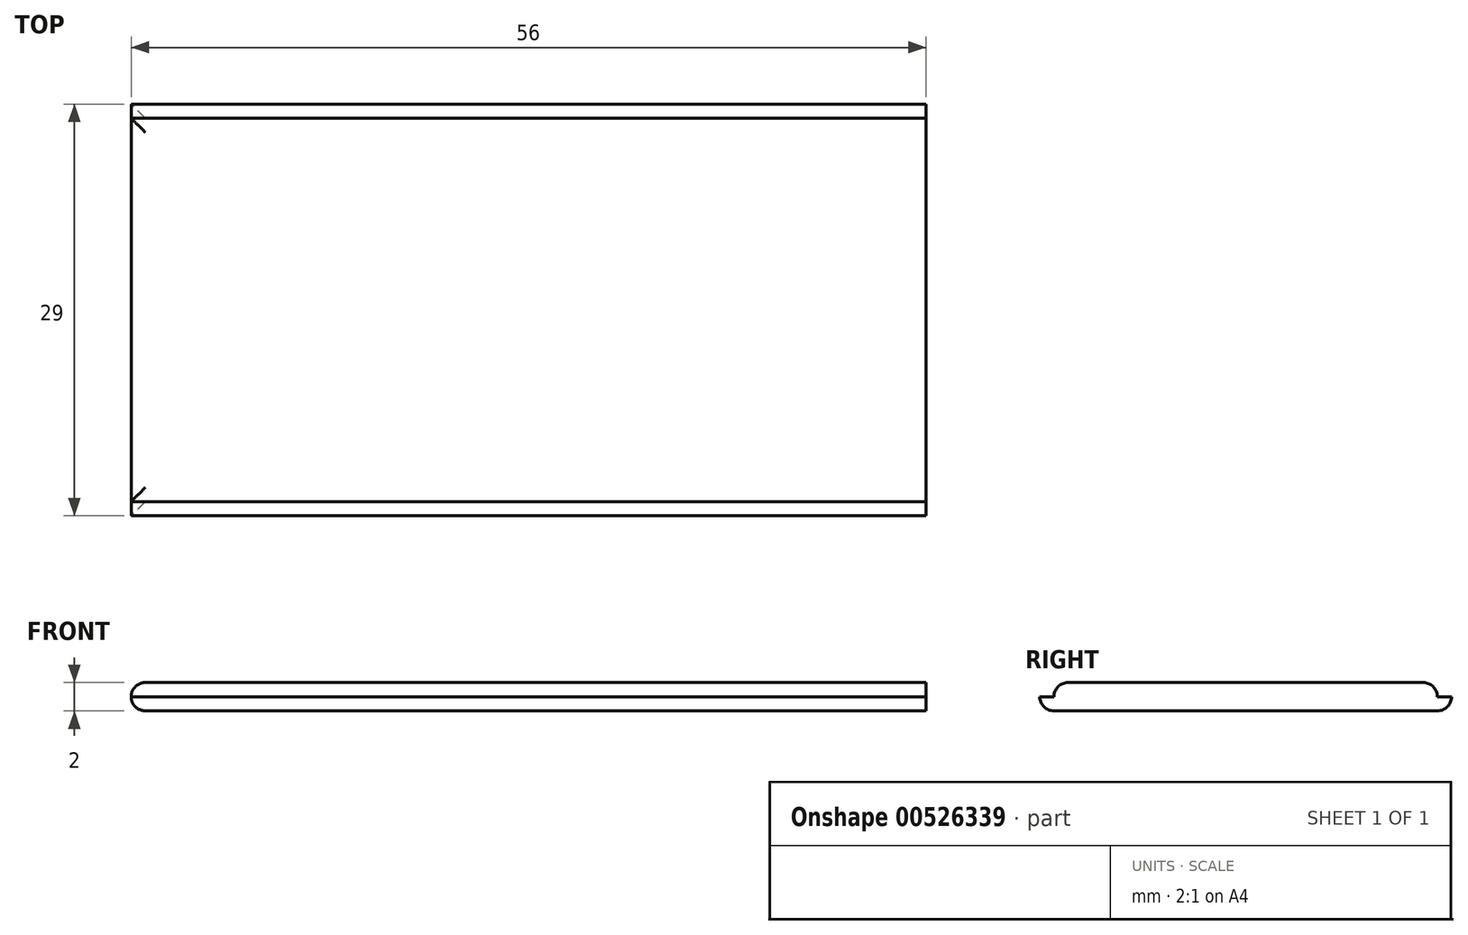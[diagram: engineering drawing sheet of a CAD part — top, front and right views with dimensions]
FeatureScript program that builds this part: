
annotation { "Feature Type Name" : "Feature", "Feature Type Description" : "" }
export const myFeature = defineFeature(function(context is Context, id is Id, definition is map)
    precondition{}
    {
        {
            var Q0;
            Q0=qCreatedBy(makeId("Right.planeOp"),FACE);
            var sketch = newSketch(context, id + "F0", { "sketchPlane" : qUnion([Q0])});
            skLineSegment(sketch, "E0", {"start": v(14.5, 0) * mm, "end": v(14.5, 1) * mm});
            skLineSegment(sketch, "E1", {"start": v(14.5, 1) * mm, "end": v(13.5, 1) * mm});
            skLineSegment(sketch, "E2", {"start": v(13.5, 1) * mm, "end": v(13.5, 2) * mm});
            skLineSegment(sketch, "E3", {"start": v(13.5, 2) * mm, "end": v(0, 2) * mm});
            skLineSegment(sketch, "E4.MirrorCS", {"start": v(-6.25, 2) * mm, "end": v(0, 2) * mm});
            skLineSegment(sketch, "E5", {"start": v(14.5, 0) * mm, "end": v(0, 0) * mm});
            skLineSegment(sketch, "E6.MirrorCS", {"start": v(-7.25, 0) * mm, "end": v(0, 0) * mm});
            skLineSegment(sketch, "E7.MirrorCS", {"start": v(-13.5, 2) * mm, "end": v(0, 2) * mm});
            skLineSegment(sketch, "E8.MirrorCS", {"start": v(-14.5, 0) * mm, "end": v(0, 0) * mm});
            skLineSegment(sketch, "E9.MirrorCS", {"start": v(-13.5, 1) * mm, "end": v(-13.5, 2) * mm});
            skLineSegment(sketch, "E10.MirrorCS", {"start": v(-14.5, 1) * mm, "end": v(-13.5, 1) * mm});
            skLineSegment(sketch, "E11.MirrorCS", {"start": v(-14.5, 0) * mm, "end": v(-14.5, 1) * mm});
            skSolve(sketch);
        }
        {
            var Q0;
            Q0=makeQuery(id+"F0.imprint","IMPRINT",FACE,{"disambiguationData":[TD([[makeQuery(id+"F0.imprint","IMPRINT",EDGE,{"derivedFrom":sQuery(id+"F0.wireOp",EDGE,"E0")}),1.0]])]});
            extrude(context, id + "F1", {"entities" : qUnion([Q0]), "depth" : 56 * mm, "offsetDistance" : 25 * mm});
        }
        {
            var Q0;
            Q0=makeQuery(id+"F1.opExtrude","SWEPT_EDGE",EDGE,{"disambiguationData":[OSD([sQuery(id+"F0.wireOp",EDGE,"E2"),sQuery(id+"F0.wireOp",EDGE,"E3")])]});
            var Q1;
            Q1=makeQuery(id+"F1.opExtrude","SWEPT_EDGE",EDGE,{"disambiguationData":[OSD([sQuery(id+"F0.wireOp",EDGE,"E7.MirrorCS"),sQuery(id+"F0.wireOp",EDGE,"E9.MirrorCS")])]});
            var Q2;
            Q2=makeQuery(id+"F1.opExtrude","SWEPT_EDGE",EDGE,{"disambiguationData":[OSD([sQuery(id+"F0.wireOp",EDGE,"E0"),sQuery(id+"F0.wireOp",EDGE,"E5")])]});
            var Q3;
            Q3=makeQuery(id+"F1.opExtrude","SWEPT_EDGE",EDGE,{"disambiguationData":[OSD([sQuery(id+"F0.wireOp",EDGE,"E8.MirrorCS"),sQuery(id+"F0.wireOp",EDGE,"E11.MirrorCS")])]});
            var Q4;
            Q4=makeQuery(id+"F1.opExtrude","CAP_EDGE",EDGE,{"disambiguationData":[OSD([sQuery(id+"F0.wireOp",EDGE,"E3"),sQuery(id+"F0.wireOp",EDGE,"E7.MirrorCS")])],"isStart":true});
            var Q5;
            Q5=makeQuery(id+"F1.opExtrude","CAP_EDGE",EDGE,{"disambiguationData":[OSD([sQuery(id+"F0.wireOp",EDGE,"E5"),sQuery(id+"F0.wireOp",EDGE,"E8.MirrorCS")])],"isStart":true});
            fillet(context, id + "F2", {"entities" : qUnion([Q0, Q1, Q2, Q3, Q4, Q5]), "radius" : 1 * mm, "tangentPropagation" : true, "allowEdgeOverflow" : false});
        }
    });
